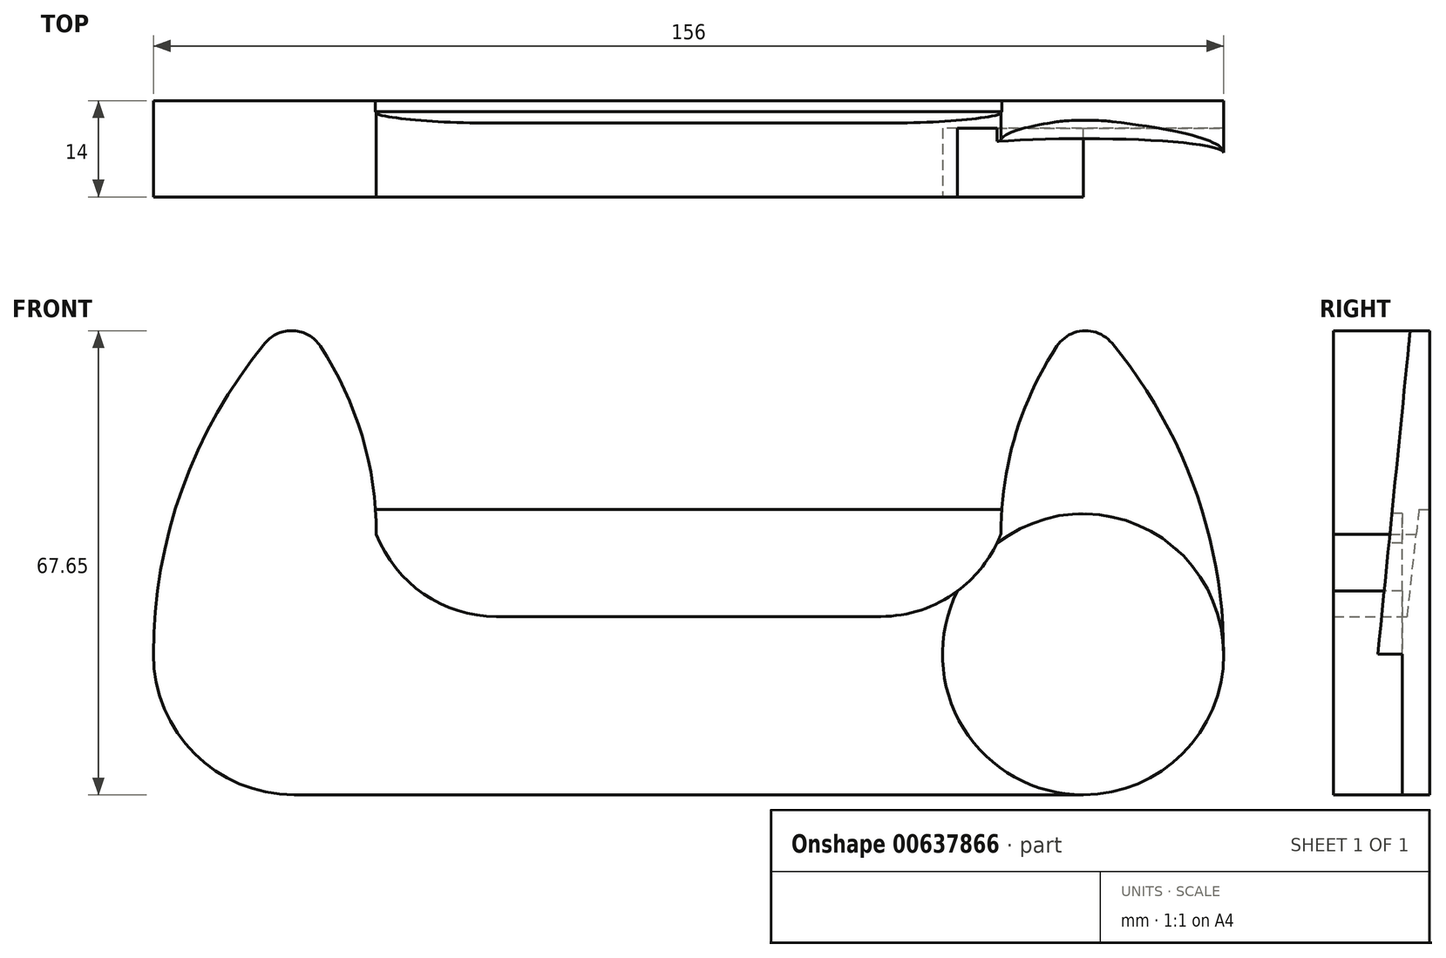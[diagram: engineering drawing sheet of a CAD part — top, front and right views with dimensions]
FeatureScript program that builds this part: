
annotation { "Feature Type Name" : "Feature", "Feature Type Description" : "" }
export const myFeature = defineFeature(function(context is Context, id is Id, definition is map)
    precondition{}
    {
        {
            var Q0;
            Q0=qCreatedBy(makeId("Front.planeOp"),FACE);
            var sketch = newSketch(context, id + "F0", { "sketchPlane" : qUnion([Q0])});
            skLineSegment(sketch, "E0.bottom", {"start": v(28, 13) * mm, "end": v(-28, 13) * mm});
            skLineSegment(sketch, "E0.top", {"start": v(28, -13) * mm, "end": v(-28, -13) * mm});
            skPoint(sketch, "E0.middle", {"position": v(0, 0) * mm});
            skLineSegment(sketch, "E1", {"start": v(-28, -13) * mm, "end": v(-57.5, -13) * mm});
            skLineSegment(sketch, "E2", {"start": v(28, -13) * mm, "end": v(57.5, -13) * mm});
            skLineSegment(sketch, "E3", {"start": v(-57.5, -13) * mm, "end": v(-57.5, 7.5) * mm, "construction": true});
            skLineSegment(sketch, "E4", {"start": v(57.5, -13) * mm, "end": v(57.5, 7.5) * mm, "construction": true});
            skLineSegment(sketch, "E5", {"start": v(57.5, 7.5) * mm, "end": v(78, 7.5) * mm, "construction": true});
            skLineSegment(sketch, "E6", {"start": v(-57.5, 7.5) * mm, "end": v(-78, 7.5) * mm, "construction": true});
            skArc(sketch, "E7", {"start": v(-78, 7.5) * mm, "mid": v(-72, -7) * mm, "end": v(-57.5, -13) * mm});
            skArc(sketch, "E8", {"start": v(57.5, -13) * mm, "mid": v(72, -7) * mm, "end": v(78, 7.5) * mm});
            skLineSegment(sketch, "E9", {"start": v(0, -13) * mm, "end": v(0.12, 25) * mm, "construction": true});
            skLineSegment(sketch, "E10.bottom", {"start": v(57.62, 25) * mm, "end": v(-57.38, 25) * mm, "construction": true});
            skLineSegment(sketch, "E10.top", {"start": v(57.62, 25) * mm, "end": v(-57.38, 25) * mm, "construction": true});
            skLineSegment(sketch, "E10.left", {"start": v(57.62, 25) * mm, "end": v(57.62, 25) * mm});
            skLineSegment(sketch, "E10.right", {"start": v(-57.38, 25) * mm, "end": v(-57.38, 25) * mm});
            skPoint(sketch, "E10.middle", {"position": v(0.12, 25) * mm});
            skLineSegment(sketch, "E11", {"start": v(-57.5, 7.5) * mm, "end": v(-57.5, 57.5) * mm, "construction": true});
            skLineSegment(sketch, "E12", {"start": v(57.5, 7.5) * mm, "end": v(57.5, 57.5) * mm, "construction": true});
            skArc(sketch, "E13", {"start": v(-45.5, 25) * mm, "mid": v(-48.6, 42.32) * mm, "end": v(-57.5, 57.5) * mm});
            skArc(sketch, "E14", {"start": v(57.5, 57.5) * mm, "mid": v(48.6, 42.32) * mm, "end": v(45.5, 25) * mm});
            skLineSegment(sketch, "E15.bottom", {"start": v(-78, 7.5) * mm, "end": v(-45.5, 7.5) * mm, "construction": true});
            skLineSegment(sketch, "E15.top", {"start": v(-78, 57.5) * mm, "end": v(-45.5, 57.5) * mm, "construction": true});
            skLineSegment(sketch, "E15.left", {"start": v(-78, 7.5) * mm, "end": v(-78, 57.5) * mm, "construction": true});
            skLineSegment(sketch, "E15.right", {"start": v(-45.5, 7.5) * mm, "end": v(-45.5, 57.5) * mm, "construction": true});
            skLineSegment(sketch, "E16.bottom", {"start": v(78, 7.5) * mm, "end": v(45.5, 7.5) * mm, "construction": true});
            skLineSegment(sketch, "E16.top", {"start": v(78, 57.5) * mm, "end": v(45.5, 57.5) * mm, "construction": true});
            skLineSegment(sketch, "E16.left", {"start": v(78, 7.5) * mm, "end": v(78, 57.5) * mm, "construction": true});
            skLineSegment(sketch, "E16.right", {"start": v(45.5, 7.5) * mm, "end": v(45.5, 57.5) * mm, "construction": true});
            skArc(sketch, "E17", {"start": v(-57.5, 57.5) * mm, "mid": v(-72.68, 34.52) * mm, "end": v(-78, 7.5) * mm});
            skArc(sketch, "E18", {"start": v(78, 7.5) * mm, "mid": v(72.68, 34.52) * mm, "end": v(57.5, 57.5) * mm});
            skArc(sketch, "E19", {"start": v(-45.5, 25) * mm, "mid": v(-38.6, 16.29) * mm, "end": v(-28, 13) * mm});
            skArc(sketch, "E20", {"start": v(28, 13) * mm, "mid": v(38.6, 16.29) * mm, "end": v(45.5, 25) * mm});
            skSolve(sketch);
        }
        {
            var Q0;
            Q0 = qSketchRegion(id + "F0", true);
            extrude(context, id + "F1", {"entities" : qUnion([Q0]), "depth" : 14 * mm, "offsetDistance" : 25 * mm});
        }
        {
            var Q0;
            Q0=makeQuery(id+"F1.opExtrude","SWEPT_EDGE",EDGE,{"disambiguationData":[OSD([sQuery(id+"F0.wireOp",EDGE,"E14"),sQuery(id+"F0.wireOp",EDGE,"E18")])]});
            var Q1;
            Q1=makeQuery(id+"F1.opExtrude","SWEPT_EDGE",EDGE,{"disambiguationData":[OSD([sQuery(id+"F0.wireOp",EDGE,"E13"),sQuery(id+"F0.wireOp",EDGE,"E17")])]});
            fillet(context, id + "F2", {"entities" : qUnion([Q0, Q1]), "radius" : 5 * mm, "tangentPropagation" : true, "allowEdgeOverflow" : false});
        }
        {
            var Q0;
            Q0=makeQuery(id+"F1.opExtrude","CAP_FACE",FACE,{"disambiguationData":[OSD([sQuery(id+"F0.wireOp",EDGE,"E0.bottom"),sQuery(id+"F0.wireOp",EDGE,"E0.top"),sQuery(id+"F0.wireOp",EDGE,"E1"),sQuery(id+"F0.wireOp",EDGE,"E2"),sQuery(id+"F0.wireOp",EDGE,"E7"),sQuery(id+"F0.wireOp",EDGE,"E8"),sQuery(id+"F0.wireOp",EDGE,"E13"),sQuery(id+"F0.wireOp",EDGE,"E14"),sQuery(id+"F0.wireOp",EDGE,"E17"),sQuery(id+"F0.wireOp",EDGE,"E18"),sQuery(id+"F0.wireOp",EDGE,"E19"),sQuery(id+"F0.wireOp",EDGE,"E20")])],"isStart":false});
            var sketch = newSketch(context, id + "F3", { "sketchPlane" : qUnion([Q0])});
            skLineSegment(sketch, "E21.bottom", {"start": v(0, -13) * mm, "end": v(57.5, -13) * mm, "construction": true});
            skLineSegment(sketch, "E21.top", {"start": v(0, 7.5) * mm, "end": v(57.5, 7.5) * mm, "construction": true});
            skLineSegment(sketch, "E21.left", {"start": v(0, -13) * mm, "end": v(0, 7.5) * mm, "construction": true});
            skLineSegment(sketch, "E21.right", {"start": v(57.5, -13) * mm, "end": v(57.5, 7.5) * mm, "construction": true});
            skCircle(sketch, "E22", {"center": v(57.5, 7.5) * mm, "radius": 20.5 * mm});
            skSolve(sketch);
        }
        {
            var Q0;
            Q0 = qSketchRegion(id + "F3", true);
            extrude(context, id + "F4", {"entities" : qUnion([Q0]), "operationType" : NewBodyOperationType.REMOVE, "oppositeDirection" : true, "depth" : 10 * mm, "offsetDistance" : 25 * mm});
        }
        {
            var Q0;
            Q0=qCreatedBy(makeId("Right.planeOp"),FACE);
            cPlane(context, id + "F5", {"entities" : qUnion([Q0]), "cplaneType" : CPlaneType.OFFSET, "offset" : 78.5 * mm, "width" : 150 * mm, "height" : 150 * mm});
        }
        {
            var Q0;
            Q0=qCreatedBy(id+"F5.planeOp",FACE);
            var sketch = newSketch(context, id + "F6", { "sketchPlane" : qUnion([Q0])});
            skLineSegment(sketch, "E23", {"start": v(-16.9, 6.1) * mm, "end": v(-16.9, 57.22) * mm});
            skLineSegment(sketch, "E24", {"start": v(-16.9, 57.22) * mm, "end": v(-2.58, 57.22) * mm});
            skLineSegment(sketch, "E25", {"start": v(-2.58, 57.22) * mm, "end": v(-7.75, 5.52) * mm});
            skLineSegment(sketch, "E26", {"start": v(-7.75, 5.52) * mm, "end": v(-16.9, 6.1) * mm});
            skSolve(sketch);
        }
        {
            var Q0;
            Q0 = qSketchRegion(id + "F6", true);
            extrude(context, id + "F7", {"entities" : qUnion([Q0]), "operationType" : NewBodyOperationType.REMOVE, "oppositeDirection" : true, "depth" : 35.5 * mm, "offsetDistance" : 25 * mm});
        }
        {
            var Q0;
            Q0=qCreatedBy(makeId("Right.planeOp"),FACE);
            cPlane(context, id + "F8", {"entities" : qUnion([Q0]), "cplaneType" : CPlaneType.OFFSET, "offset" : 57 * mm, "width" : 150 * mm, "height" : 150 * mm});
        }
        {
            var Q0;
            Q0=qCreatedBy(id+"F8.planeOp",FACE);
            var sketch = newSketch(context, id + "F9", { "sketchPlane" : qUnion([Q0])});
            skLineSegment(sketch, "E27", {"start": v(0, 6.54) * mm, "end": v(0, 28.56) * mm});
            skLineSegment(sketch, "E28", {"start": v(0, 28.56) * mm, "end": v(-1.55, 28.56) * mm});
            skLineSegment(sketch, "E29", {"start": v(-1.55, 28.56) * mm, "end": v(-3.52, 10.54) * mm});
            skLineSegment(sketch, "E30", {"start": v(-3.52, 10.54) * mm, "end": v(-3.52, 0) * mm});
            skLineSegment(sketch, "E31", {"start": v(-3.52, 0) * mm, "end": v(0, 0) * mm});
            skLineSegment(sketch, "E32", {"start": v(0, 0) * mm, "end": v(0, 6.54) * mm});
            skSolve(sketch);
        }
        {
            var Q0;
            Q0 = qSketchRegion(id + "F9", true);
            extrude(context, id + "F10", {"entities" : qUnion([Q0]), "operationType" : NewBodyOperationType.ADD, "oppositeDirection" : true, "depth" : 106.1 * mm, "offsetDistance" : 25 * mm});
        }
    });
